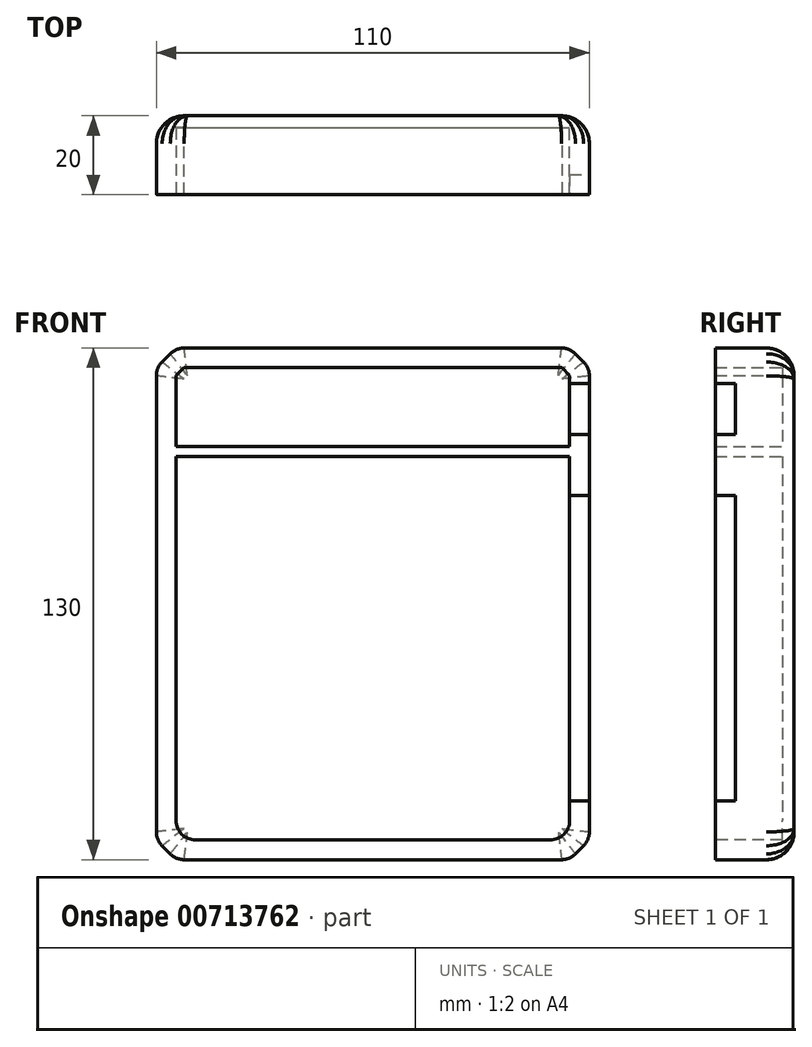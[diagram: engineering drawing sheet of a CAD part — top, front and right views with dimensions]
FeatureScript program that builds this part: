
annotation { "Feature Type Name" : "Feature", "Feature Type Description" : "" }
export const myFeature = defineFeature(function(context is Context, id is Id, definition is map)
    precondition{}
    {
        {
            var Q0;
            Q0=qCreatedBy(makeId("Front.planeOp"),FACE);
            var sketch = newSketch(context, id + "F0", { "sketchPlane" : qUnion([Q0])});
            skLineSegment(sketch, "E0.bottom", {"start": v(55, -65) * mm, "end": v(-55, -65) * mm});
            skLineSegment(sketch, "E0.top", {"start": v(55, 65) * mm, "end": v(-55, 65) * mm});
            skLineSegment(sketch, "E0.left", {"start": v(55, -65) * mm, "end": v(55, 65) * mm});
            skLineSegment(sketch, "E0.right", {"start": v(-55, -65) * mm, "end": v(-55, 65) * mm});
            skPoint(sketch, "E0.middle", {"position": v(0, 0) * mm});
            skSolve(sketch);
        }
        {
            var Q0;
            Q0=makeQuery(id+"F0.imprint","IMPRINT",FACE,{"disambiguationData":[TD([[makeQuery(id+"F0.imprint","IMPRINT",EDGE,{"derivedFrom":sQuery(id+"F0.wireOp",EDGE,"E0.bottom")}),-1.0]])]});
            extrude(context, id + "F1", {"entities" : qUnion([Q0]), "depth" : 20 * mm, "offsetDistance" : 25 * mm});
        }
        {
            var Q0;
            Q0=makeQuery(id+"F1.opExtrude","CAP_FACE",FACE,{"disambiguationData":[OSD([sQuery(id+"F0.wireOp",EDGE,"E0.bottom"),sQuery(id+"F0.wireOp",EDGE,"E0.top"),sQuery(id+"F0.wireOp",EDGE,"E0.left"),sQuery(id+"F0.wireOp",EDGE,"E0.right")])],"isStart":false});
            var sketch = newSketch(context, id + "F2", { "sketchPlane" : qUnion([Q0])});
            skLineSegment(sketch, "E1.bottom", {"start": v(-50, 60) * mm, "end": v(50, 60) * mm});
            skLineSegment(sketch, "E1.top", {"start": v(-50, -60) * mm, "end": v(50, -60) * mm});
            skLineSegment(sketch, "E1.left", {"start": v(-50, 60) * mm, "end": v(-50, -60) * mm});
            skLineSegment(sketch, "E1.right", {"start": v(50, 60) * mm, "end": v(50, -60) * mm});
            skSolve(sketch);
        }
        {
            var Q0;
            Q0=makeQuery(id+"F2.imprint","IMPRINT",FACE,{"disambiguationData":[TD([[makeQuery(id+"F2.imprint","IMPRINT",EDGE,{"derivedFrom":sQuery(id+"F2.wireOp",EDGE,"E1.bottom")}),-1.0]])]});
            extrude(context, id + "F3", {"entities" : qUnion([Q0]), "operationType" : NewBodyOperationType.REMOVE, "oppositeDirection" : true, "depth" : 17 * mm, "offsetDistance" : 25 * mm});
        }
        {
            var Q0;
            Q0=makeQuery(id+"F3.boolean.opBoolean","COPY",FACE,{"derivedFrom":makeQuery(id+"F3.opExtrude","CAP_FACE",FACE,{"disambiguationData":[OSD([sQuery(id+"F2.wireOp",EDGE,"E1.bottom"),sQuery(id+"F2.wireOp",EDGE,"E1.top"),sQuery(id+"F2.wireOp",EDGE,"E1.left"),sQuery(id+"F2.wireOp",EDGE,"E1.right")])],"isStart":false})});
            var sketch = newSketch(context, id + "F4", { "sketchPlane" : qUnion([Q0])});
            skLineSegment(sketch, "E2.bottom", {"start": v(-50, 37.5) * mm, "end": v(50, 37.5) * mm});
            skLineSegment(sketch, "E2.top", {"start": v(-50, 40) * mm, "end": v(50, 40) * mm});
            skLineSegment(sketch, "E2.left", {"start": v(-50, 37.5) * mm, "end": v(-50, 40) * mm});
            skLineSegment(sketch, "E2.right", {"start": v(50, 37.5) * mm, "end": v(50, 40) * mm});
            skSolve(sketch);
        }
        {
            var Q0;
            Q0 = qSketchRegion(id + "F4", true);
            var Q1;
            Q1=makeQuery(id+"F1.opExtrude","CAP_FACE",FACE,{"disambiguationData":[OSD([sQuery(id+"F0.wireOp",EDGE,"E0.bottom"),sQuery(id+"F0.wireOp",EDGE,"E0.top"),sQuery(id+"F0.wireOp",EDGE,"E0.left"),sQuery(id+"F0.wireOp",EDGE,"E0.right")])],"isStart":false});
            extrude(context, id + "F5", {"entities" : qUnion([Q0]), "operationType" : NewBodyOperationType.ADD, "endBound" : BoundingType.UP_TO_SURFACE, "depth" : 25 * mm, "endBoundEntityFace" : qUnion([Q1]), "offsetDistance" : 25 * mm});
        }
        {
            var Q0;
            Q0=makeQuery(id+"F1.opExtrude","SWEPT_EDGE",EDGE,{"disambiguationData":[OSD([sQuery(id+"F0.wireOp",EDGE,"E0.top"),sQuery(id+"F0.wireOp",EDGE,"E0.left")])]});
            var Q1;
            Q1=makeQuery(id+"F1.opExtrude","SWEPT_EDGE",EDGE,{"disambiguationData":[OSD([sQuery(id+"F0.wireOp",EDGE,"E0.top"),sQuery(id+"F0.wireOp",EDGE,"E0.right")])]});
            var Q2;
            Q2=makeQuery(id+"F1.opExtrude","SWEPT_EDGE",EDGE,{"disambiguationData":[OSD([sQuery(id+"F0.wireOp",EDGE,"E0.bottom"),sQuery(id+"F0.wireOp",EDGE,"E0.left")])]});
            var Q3;
            Q3=makeQuery(id+"F1.opExtrude","SWEPT_EDGE",EDGE,{"disambiguationData":[OSD([sQuery(id+"F0.wireOp",EDGE,"E0.bottom"),sQuery(id+"F0.wireOp",EDGE,"E0.right")])]});
            chamfer(context, id + "F6", {"entities" : qUnion([Q0, Q1, Q2, Q3]), "width" : 5 * mm, "tangentPropagation" : true});
        }
        {
            var Q0;
            Q0=makeQuery(id+"F3.boolean.opBoolean","COPY",EDGE,{"derivedFrom":makeQuery(id+"F3.opExtrude","SWEPT_EDGE",EDGE,{"disambiguationData":[OSD([sQuery(id+"F2.wireOp",EDGE,"E1.bottom"),sQuery(id+"F2.wireOp",EDGE,"E1.right")])]})});
            var Q1;
            Q1=makeQuery(id+"F3.boolean.opBoolean","COPY",EDGE,{"derivedFrom":makeQuery(id+"F3.opExtrude","SWEPT_EDGE",EDGE,{"disambiguationData":[OSD([sQuery(id+"F2.wireOp",EDGE,"E1.bottom"),sQuery(id+"F2.wireOp",EDGE,"E1.left")])]})});
            chamfer(context, id + "F7", {"entities" : qUnion([Q0, Q1]), "width" : 2 * mm, "tangentPropagation" : true});
        }
        {
            var Q0;
            Q0=makeQuery(id+"F1.opExtrude","CAP_FACE",FACE,{"disambiguationData":[OSD([sQuery(id+"F0.wireOp",EDGE,"E0.bottom"),sQuery(id+"F0.wireOp",EDGE,"E0.top"),sQuery(id+"F0.wireOp",EDGE,"E0.left"),sQuery(id+"F0.wireOp",EDGE,"E0.right")])],"isStart":true});
            fillet(context, id + "F8", {"entities" : qUnion([Q0]), "radius" : 7 * mm, "tangentPropagation" : true, "allowEdgeOverflow" : false});
        }
        {
            var Q0;
            {var subQ0=sQuery(id+"F0.wireOp",EDGE,"E0.right");Q0=makeQuery(id+"F6.opChamfer","BLEND_EDGE",EDGE,{"blendedFrom":[makeQuery(id+"F1.opExtrude","SWEPT_EDGE",EDGE,{"disambiguationData":[OSD([sQuery(id+"F0.wireOp",EDGE,"E0.bottom"),subQ0])]}),makeQuery(id+"F1.opExtrude","SWEPT_FACE",FACE,{"disambiguationData":[OSD([subQ0])]})],"blendedInto":[makeQuery(id+"F1.opExtrude","SWEPT_FACE",FACE,{"disambiguationData":[OSD([subQ0])]})]});}
            var Q1;
            {var subQ0=sQuery(id+"F0.wireOp",EDGE,"E0.bottom");Q1=makeQuery(id+"F6.opChamfer","BLEND_EDGE",EDGE,{"blendedFrom":[makeQuery(id+"F1.opExtrude","SWEPT_EDGE",EDGE,{"disambiguationData":[OSD([subQ0,sQuery(id+"F0.wireOp",EDGE,"E0.right")])]}),makeQuery(id+"F1.opExtrude","SWEPT_FACE",FACE,{"disambiguationData":[OSD([subQ0])]})],"blendedInto":[makeQuery(id+"F1.opExtrude","SWEPT_FACE",FACE,{"disambiguationData":[OSD([subQ0])]})]});}
            var Q2;
            {var subQ0=sQuery(id+"F0.wireOp",EDGE,"E0.left");Q2=makeQuery(id+"F6.opChamfer","BLEND_EDGE",EDGE,{"blendedFrom":[makeQuery(id+"F1.opExtrude","SWEPT_EDGE",EDGE,{"disambiguationData":[OSD([sQuery(id+"F0.wireOp",EDGE,"E0.bottom"),subQ0])]}),makeQuery(id+"F1.opExtrude","SWEPT_FACE",FACE,{"disambiguationData":[OSD([subQ0])]})],"blendedInto":[makeQuery(id+"F1.opExtrude","SWEPT_FACE",FACE,{"disambiguationData":[OSD([subQ0])]})]});}
            var Q3;
            {var subQ0=sQuery(id+"F0.wireOp",EDGE,"E0.bottom");Q3=makeQuery(id+"F6.opChamfer","BLEND_EDGE",EDGE,{"blendedFrom":[makeQuery(id+"F1.opExtrude","SWEPT_EDGE",EDGE,{"disambiguationData":[OSD([subQ0,sQuery(id+"F0.wireOp",EDGE,"E0.left")])]}),makeQuery(id+"F1.opExtrude","SWEPT_FACE",FACE,{"disambiguationData":[OSD([subQ0])]})],"blendedInto":[makeQuery(id+"F1.opExtrude","SWEPT_FACE",FACE,{"disambiguationData":[OSD([subQ0])]})]});}
            var Q4;
            {var subQ0=sQuery(id+"F0.wireOp",EDGE,"E0.top");Q4=makeQuery(id+"F6.opChamfer","BLEND_EDGE",EDGE,{"blendedFrom":[makeQuery(id+"F1.opExtrude","SWEPT_EDGE",EDGE,{"disambiguationData":[OSD([subQ0,sQuery(id+"F0.wireOp",EDGE,"E0.left")])]}),makeQuery(id+"F1.opExtrude","SWEPT_FACE",FACE,{"disambiguationData":[OSD([subQ0])]})],"blendedInto":[makeQuery(id+"F1.opExtrude","SWEPT_FACE",FACE,{"disambiguationData":[OSD([subQ0])]})]});}
            var Q5;
            {var subQ0=sQuery(id+"F0.wireOp",EDGE,"E0.left");Q5=makeQuery(id+"F6.opChamfer","BLEND_EDGE",EDGE,{"blendedFrom":[makeQuery(id+"F1.opExtrude","SWEPT_EDGE",EDGE,{"disambiguationData":[OSD([sQuery(id+"F0.wireOp",EDGE,"E0.top"),subQ0])]}),makeQuery(id+"F1.opExtrude","SWEPT_FACE",FACE,{"disambiguationData":[OSD([subQ0])]})],"blendedInto":[makeQuery(id+"F1.opExtrude","SWEPT_FACE",FACE,{"disambiguationData":[OSD([subQ0])]})]});}
            fillet(context, id + "F9", {"entities" : qUnion([Q0, Q1, Q2, Q3, Q4, Q5]), "radius" : 5 * mm, "tangentPropagation" : true, "allowEdgeOverflow" : false});
        }
        {
            var Q0;
            {var subQ0=sQuery(id+"F0.wireOp",EDGE,"E0.top");Q0=makeQuery(id+"F6.opChamfer","BLEND_EDGE",EDGE,{"blendedFrom":[makeQuery(id+"F1.opExtrude","SWEPT_EDGE",EDGE,{"disambiguationData":[OSD([subQ0,sQuery(id+"F0.wireOp",EDGE,"E0.right")])]}),makeQuery(id+"F1.opExtrude","SWEPT_FACE",FACE,{"disambiguationData":[OSD([subQ0])]})],"blendedInto":[makeQuery(id+"F1.opExtrude","SWEPT_FACE",FACE,{"disambiguationData":[OSD([subQ0])]})]});}
            var Q1;
            {var subQ0=sQuery(id+"F0.wireOp",EDGE,"E0.right");Q1=makeQuery(id+"F6.opChamfer","BLEND_EDGE",EDGE,{"blendedFrom":[makeQuery(id+"F1.opExtrude","SWEPT_EDGE",EDGE,{"disambiguationData":[OSD([sQuery(id+"F0.wireOp",EDGE,"E0.top"),subQ0])]}),makeQuery(id+"F1.opExtrude","SWEPT_FACE",FACE,{"disambiguationData":[OSD([subQ0])]})],"blendedInto":[makeQuery(id+"F1.opExtrude","SWEPT_FACE",FACE,{"disambiguationData":[OSD([subQ0])]})]});}
            fillet(context, id + "F10", {"entities" : qUnion([Q0, Q1]), "radius" : 5 * mm, "tangentPropagation" : true, "allowEdgeOverflow" : false});
        }
        {
            var Q0;
            Q0=makeQuery(id+"F3.boolean.opBoolean","COPY",EDGE,{"derivedFrom":makeQuery(id+"F3.opExtrude","SWEPT_EDGE",EDGE,{"disambiguationData":[OSD([sQuery(id+"F2.wireOp",EDGE,"E1.top"),sQuery(id+"F2.wireOp",EDGE,"E1.left")])]})});
            var Q1;
            Q1=makeQuery(id+"F3.boolean.opBoolean","COPY",EDGE,{"derivedFrom":makeQuery(id+"F3.opExtrude","SWEPT_EDGE",EDGE,{"disambiguationData":[OSD([sQuery(id+"F2.wireOp",EDGE,"E1.top"),sQuery(id+"F2.wireOp",EDGE,"E1.right")])]})});
            fillet(context, id + "F11", {"entities" : qUnion([Q0, Q1]), "radius" : 5 * mm, "tangentPropagation" : true, "allowEdgeOverflow" : false});
        }
        {
            var Q0;
            {var subQ0=sQuery(id+"F0.wireOp",EDGE,"E0.right");var subQ1=sQuery(id+"F0.wireOp",EDGE,"E0.left");var subQ2=sQuery(id+"F0.wireOp",EDGE,"E0.top");var subQ3=sQuery(id+"F0.wireOp",EDGE,"E0.bottom");Q0=makeQuery(id+"F5.boolean.opBoolean","MERGE",FACE,{"derivedFrom":[makeQuery(id+"F1.opExtrude","CAP_FACE",FACE,{"disambiguationData":[OSD([subQ3,subQ2,subQ1,subQ0])],"isStart":false}),makeQuery(id+"F5.opExtrude","CAP_FACE",FACE,{"disambiguationData":[OSD([subQ3,subQ2,subQ1,subQ0])],"isStart":false})]});}
            var sketch = newSketch(context, id + "F12", { "sketchPlane" : qUnion([Q0])});
            skLineSegment(sketch, "E3.bottom", {"start": v(50, 27.5) * mm, "end": v(55, 27.5) * mm});
            skLineSegment(sketch, "E3.top", {"start": v(50, -50) * mm, "end": v(55, -50) * mm});
            skLineSegment(sketch, "E3.left", {"start": v(50, 27.5) * mm, "end": v(50, -50) * mm});
            skLineSegment(sketch, "E3.right", {"start": v(55, 27.5) * mm, "end": v(55, -50) * mm});
            skSolve(sketch);
        }
        {
            var Q0;
            Q0 = qSketchRegion(id + "F12", true);
            extrude(context, id + "F13", {"entities" : qUnion([Q0]), "operationType" : NewBodyOperationType.REMOVE, "oppositeDirection" : true, "depth" : 5.1 * mm, "offsetDistance" : 25 * mm});
        }
        {
            var Q0;
            {var subQ0=sQuery(id+"F0.wireOp",EDGE,"E0.right");var subQ1=sQuery(id+"F0.wireOp",EDGE,"E0.left");var subQ2=sQuery(id+"F0.wireOp",EDGE,"E0.top");var subQ3=sQuery(id+"F0.wireOp",EDGE,"E0.bottom");Q0=makeQuery(id+"F5.boolean.opBoolean","MERGE",FACE,{"derivedFrom":[makeQuery(id+"F1.opExtrude","CAP_FACE",FACE,{"disambiguationData":[OSD([subQ3,subQ2,subQ1,subQ0])],"isStart":false}),makeQuery(id+"F5.opExtrude","CAP_FACE",FACE,{"disambiguationData":[OSD([subQ3,subQ2,subQ1,subQ0])],"isStart":false})]});}
            var sketch = newSketch(context, id + "F14", { "sketchPlane" : qUnion([Q0])});
            skLineSegment(sketch, "E4.bottom", {"start": v(50, 56) * mm, "end": v(55, 56) * mm});
            skLineSegment(sketch, "E4.top", {"start": v(50, 43) * mm, "end": v(55, 43) * mm});
            skLineSegment(sketch, "E4.left", {"start": v(50, 56) * mm, "end": v(50, 43) * mm});
            skLineSegment(sketch, "E4.right", {"start": v(55, 56) * mm, "end": v(55, 43) * mm});
            skSolve(sketch);
        }
        {
            var Q0;
            Q0 = qSketchRegion(id + "F14", true);
            extrude(context, id + "F15", {"entities" : qUnion([Q0]), "operationType" : NewBodyOperationType.REMOVE, "oppositeDirection" : true, "depth" : 5.1 * mm, "offsetDistance" : 25 * mm});
        }
    });
